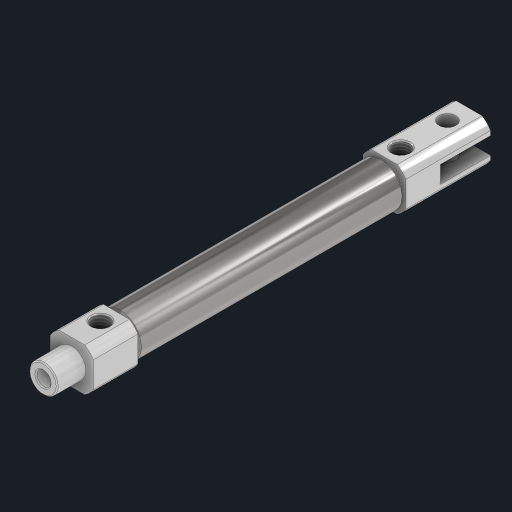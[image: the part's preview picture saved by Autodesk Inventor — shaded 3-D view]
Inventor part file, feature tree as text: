
AUTODESK INVENTOR PART (.ipt)
format: ipt  version: 2023 (Build 270158030, 158C)  size: 207,360 bytes
history: mixed  units: in
note: dims shown in document units (in); Inventor stores cm internally (conversion verified against a paired STEP export)
features: thread x2, extrude x1, sketch x1, other x1, imported_body x1
ambient origin geometry x8: Origin, YZ Plane, XZ Plane, XY Plane, X Axis, Y Axis, Z Axis, Center Point
bodies: Solid1 (imported_parasolid)
feature tree (6):
  thread  "Thread1"  [1 undecoded]
  thread  "Thread2"  [1 undecoded]
  extrude  "Extrusion3"  [1 undecoded]
  sketch  "Sketch3"  dims[d8=0.0in d9=0.0in]
  other  "DetailChamfer"
  imported_body  NMx_Import_Brep_tag  [imported B-rep: ~35 faces, bbox_mm=[12.0, 12.0, 104.093597]]
note: 3 required parameter values undecoded (feature->parameter linkage not recoverable at this tier; creation-order binding heuristic only, values carry confidence <= 0.55)
